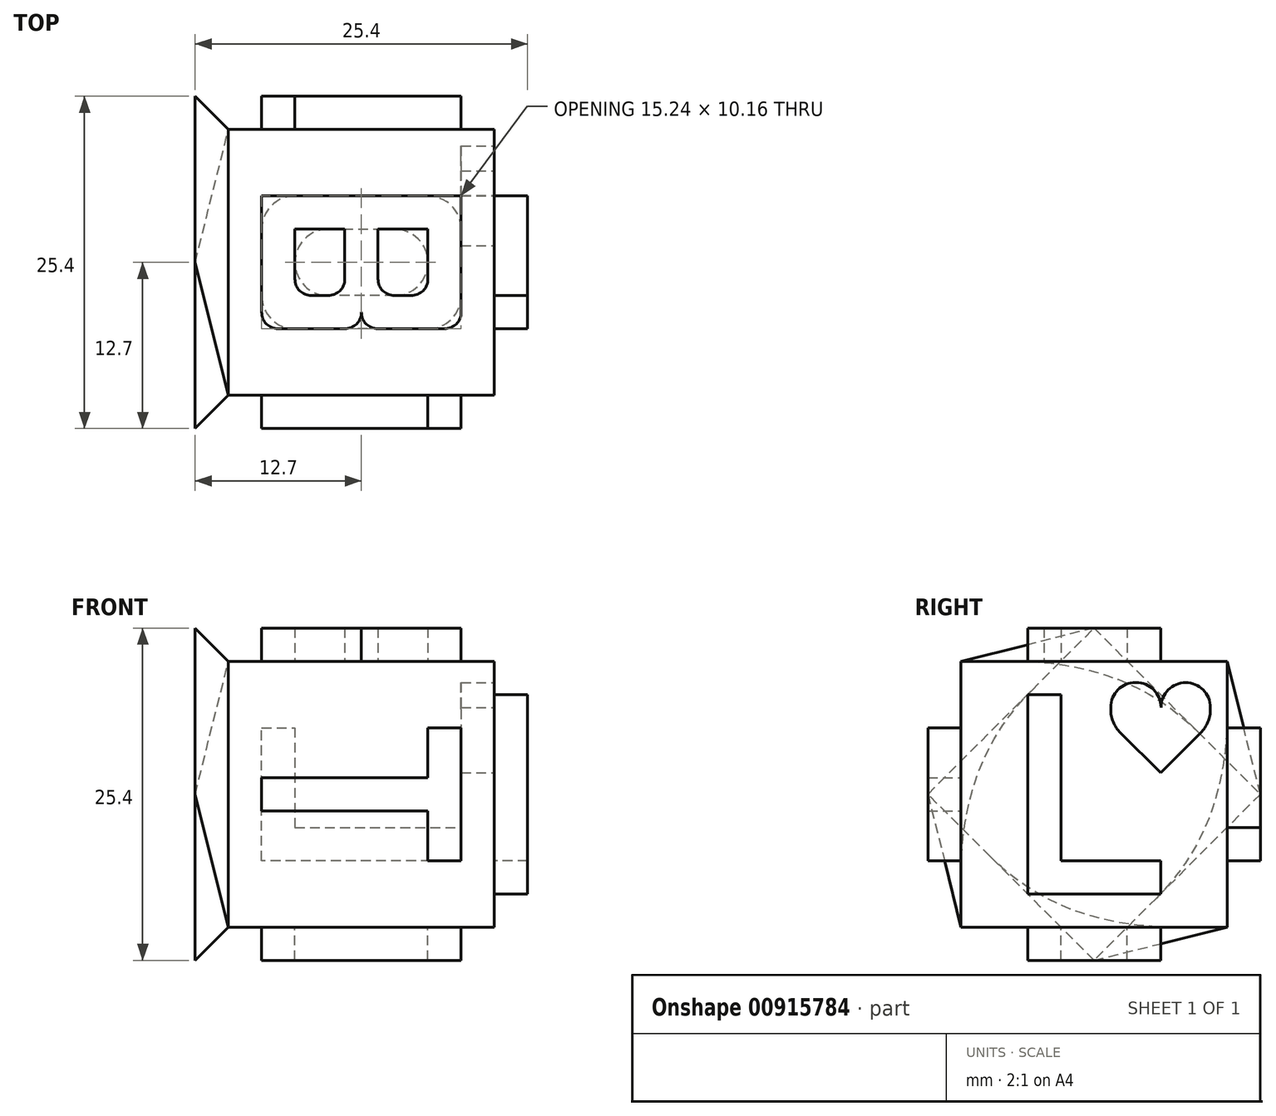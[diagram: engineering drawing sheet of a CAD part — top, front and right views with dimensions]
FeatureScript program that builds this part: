
annotation { "Feature Type Name" : "Feature", "Feature Type Description" : "" }
export const myFeature = defineFeature(function(context is Context, id is Id, definition is map)
    precondition{}
    {
        {
            var Q0;
            Q0=qCreatedBy(makeId("Right.planeOp"),FACE);
            var sketch = newSketch(context, id + "F0", { "sketchPlane" : qUnion([Q0])});
            skLineSegment(sketch, "E0.bottom", {"start": v(10.16, -10.16) * mm, "end": v(-10.16, -10.16) * mm});
            skLineSegment(sketch, "E0.top", {"start": v(10.16, 10.16) * mm, "end": v(-10.16, 10.16) * mm});
            skLineSegment(sketch, "E0.left", {"start": v(10.16, -10.16) * mm, "end": v(10.16, 10.16) * mm});
            skLineSegment(sketch, "E0.right", {"start": v(-10.16, -10.16) * mm, "end": v(-10.16, 10.16) * mm});
            skPoint(sketch, "E0.middle", {"position": v(0, 0) * mm});
            skSolve(sketch);
        }
        {
            var Q0;
            Q0=makeQuery(id+"F0.imprint","IMPRINT",FACE,{"disambiguationData":[TD([[makeQuery(id+"F0.imprint","IMPRINT",EDGE,{"derivedFrom":sQuery(id+"F0.wireOp",EDGE,"E0.bottom")}),-1.0]])]});
            extrude(context, id + "F1", {"entities" : qUnion([Q0]), "depth" : 20.32 * mm, "offsetDistance" : 25.4 * mm});
        }
        {
            var Q0;
            Q0=makeQuery(id+"F1.opExtrude","CAP_FACE",FACE,{"disambiguationData":[OSD([sQuery(id+"F0.wireOp",EDGE,"E0.bottom"),sQuery(id+"F0.wireOp",EDGE,"E0.top"),sQuery(id+"F0.wireOp",EDGE,"E0.left"),sQuery(id+"F0.wireOp",EDGE,"E0.right")])],"isStart":false});
            var sketch = newSketch(context, id + "F2", { "sketchPlane" : qUnion([Q0])});
            skLineSegment(sketch, "E1", {"start": v(-5.08, 7.62) * mm, "end": v(-5.08, -7.62) * mm});
            skLineSegment(sketch, "E2", {"start": v(-5.08, -7.62) * mm, "end": v(5.08, -7.62) * mm});
            skLineSegment(sketch, "E3", {"start": v(5.08, -7.62) * mm, "end": v(5.08, -5.08) * mm});
            skLineSegment(sketch, "E4", {"start": v(5.08, -5.08) * mm, "end": v(-2.54, -5.08) * mm});
            skLineSegment(sketch, "E5", {"start": v(-2.54, -5.08) * mm, "end": v(-2.54, 7.62) * mm});
            skLineSegment(sketch, "E6", {"start": v(-2.54, 7.62) * mm, "end": v(-5.08, 7.62) * mm});
            skSolve(sketch);
        }
        {
            var Q0;
            Q0=makeQuery(id+"F2.imprint","IMPRINT",FACE,{"disambiguationData":[TD([[makeQuery(id+"F2.imprint","IMPRINT",EDGE,{"derivedFrom":sQuery(id+"F2.wireOp",EDGE,"E1")}),1.0]])]});
            extrude(context, id + "F3", {"entities" : qUnion([Q0]), "operationType" : NewBodyOperationType.ADD, "depth" : 2.54 * mm, "offsetDistance" : 25.4 * mm});
        }
        {
            var Q0;
            Q0=makeQuery(id+"F1.opExtrude","SWEPT_FACE",FACE,{"disambiguationData":[OSD([sQuery(id+"F0.wireOp",EDGE,"E0.bottom")])]});
            var sketch = newSketch(context, id + "F4", { "sketchPlane" : qUnion([Q0])});
            skLineSegment(sketch, "E7", {"start": v(15.24, 5.08) * mm, "end": v(5.08, 5.08) * mm});
            skLineSegment(sketch, "E8", {"start": v(2.54, 2.54) * mm, "end": v(2.54, -2.54) * mm});
            skLineSegment(sketch, "E9", {"start": v(5.08, -5.08) * mm, "end": v(15.24, -5.08) * mm});
            skLineSegment(sketch, "E10", {"start": v(17.78, -2.54) * mm, "end": v(17.78, 2.54) * mm});
            skLineSegment(sketch, "E11", {"start": v(12.7, 2.54) * mm, "end": v(7.62, 2.54) * mm});
            skLineSegment(sketch, "E12", {"start": v(5.08, 0) * mm, "end": v(5.08, 0) * mm});
            skLineSegment(sketch, "E13", {"start": v(7.62, -2.54) * mm, "end": v(12.7, -2.54) * mm});
            skLineSegment(sketch, "E14", {"start": v(15.24, 0) * mm, "end": v(15.24, 0) * mm});
            skPoint(sketch, "E15.visualSharp", {"position": v(17.78, 5.08) * mm});
            skArc(sketch, "E15.filletArc", {"start": v(17.78, 2.54) * mm, "mid": v(17.04, 4.34) * mm, "end": v(15.24, 5.08) * mm});
            skPoint(sketch, "E16.visualSharp", {"position": v(17.78, -5.08) * mm});
            skArc(sketch, "E16.filletArc", {"start": v(15.24, -5.08) * mm, "mid": v(17.04, -4.34) * mm, "end": v(17.78, -2.54) * mm});
            skPoint(sketch, "E17.visualSharp", {"position": v(2.54, -5.08) * mm});
            skArc(sketch, "E17.filletArc", {"start": v(2.54, -2.54) * mm, "mid": v(3.28, -4.34) * mm, "end": v(5.08, -5.08) * mm});
            skPoint(sketch, "E18.visualSharp", {"position": v(2.54, 5.08) * mm});
            skArc(sketch, "E18.filletArc", {"start": v(5.08, 5.08) * mm, "mid": v(3.28, 4.34) * mm, "end": v(2.54, 2.54) * mm});
            skArc(sketch, "E19.filletArc", {"start": v(7.62, 2.54) * mm, "mid": v(5.82, 1.8) * mm, "end": v(5.08, 0) * mm});
            skArc(sketch, "E20.filletArc", {"start": v(5.08, 0) * mm, "mid": v(5.82, -1.8) * mm, "end": v(7.62, -2.54) * mm});
            skArc(sketch, "E21.filletArc", {"start": v(12.7, -2.54) * mm, "mid": v(14.5, -1.8) * mm, "end": v(15.24, 0) * mm});
            skArc(sketch, "E22.filletArc", {"start": v(15.24, 0) * mm, "mid": v(14.5, 1.8) * mm, "end": v(12.7, 2.54) * mm});
            skSolve(sketch);
        }
        {
            var Q0;
            Q0=makeQuery(id+"F4.imprint","IMPRINT",FACE,{"disambiguationData":[TD([[makeQuery(id+"F4.imprint","IMPRINT",EDGE,{"derivedFrom":sQuery(id+"F4.wireOp",EDGE,"E7")}),1.0]])]});
            extrude(context, id + "F5", {"entities" : qUnion([Q0]), "operationType" : NewBodyOperationType.ADD, "depth" : 2.54 * mm, "offsetDistance" : 25.4 * mm});
        }
        {
            var Q0;
            Q0=makeQuery(id+"F1.opExtrude","SWEPT_FACE",FACE,{"disambiguationData":[OSD([sQuery(id+"F0.wireOp",EDGE,"E0.right")])]});
            var sketch = newSketch(context, id + "F6", { "sketchPlane" : qUnion([Q0])});
            skLineSegment(sketch, "E23", {"start": v(2.54, 1.27) * mm, "end": v(15.24, 1.27) * mm});
            skLineSegment(sketch, "E24", {"start": v(15.24, 1.27) * mm, "end": v(15.24, 5.08) * mm});
            skLineSegment(sketch, "E25", {"start": v(15.24, 5.08) * mm, "end": v(17.78, 5.08) * mm});
            skLineSegment(sketch, "E26", {"start": v(17.78, 5.08) * mm, "end": v(17.78, -5.08) * mm});
            skLineSegment(sketch, "E27", {"start": v(17.78, -5.08) * mm, "end": v(15.24, -5.08) * mm});
            skLineSegment(sketch, "E28", {"start": v(15.24, -5.08) * mm, "end": v(15.24, -1.27) * mm});
            skLineSegment(sketch, "E29", {"start": v(15.24, -1.27) * mm, "end": v(2.54, -1.27) * mm});
            skLineSegment(sketch, "E30", {"start": v(2.54, -1.27) * mm, "end": v(2.54, 1.27) * mm});
            skSolve(sketch);
        }
        {
            var Q0;
            Q0=makeQuery(id+"F6.imprint","IMPRINT",FACE,{"disambiguationData":[TD([[makeQuery(id+"F6.imprint","IMPRINT",EDGE,{"derivedFrom":sQuery(id+"F6.wireOp",EDGE,"E23")}),-1.0]])]});
            extrude(context, id + "F7", {"entities" : qUnion([Q0]), "operationType" : NewBodyOperationType.ADD, "depth" : 2.54 * mm, "offsetDistance" : 25.4 * mm});
        }
        {
            var Q0;
            Q0=makeQuery(id+"F1.opExtrude","SWEPT_FACE",FACE,{"disambiguationData":[OSD([sQuery(id+"F0.wireOp",EDGE,"E0.top")])]});
            var sketch = newSketch(context, id + "F8", { "sketchPlane" : qUnion([Q0])});
            skLineSegment(sketch, "E31", {"start": v(17.78, 5.08) * mm, "end": v(2.54, 5.08) * mm});
            skLineSegment(sketch, "E32", {"start": v(2.54, 5.08) * mm, "end": v(2.54, -3.81) * mm});
            skLineSegment(sketch, "E33", {"start": v(3.81, -5.08) * mm, "end": v(8.9, -5.08) * mm});
            skLineSegment(sketch, "E34", {"start": v(10.16, -3.81) * mm, "end": v(10.16, 5.08) * mm});
            skLineSegment(sketch, "E35", {"start": v(11.43, -5.08) * mm, "end": v(16.51, -5.08) * mm});
            skLineSegment(sketch, "E36", {"start": v(17.78, -3.81) * mm, "end": v(17.78, 5.08) * mm});
            skLineSegment(sketch, "E37", {"start": v(11.43, 2.54) * mm, "end": v(15.24, 2.54) * mm});
            skLineSegment(sketch, "E38", {"start": v(15.24, 2.54) * mm, "end": v(15.24, -1.27) * mm});
            skLineSegment(sketch, "E39", {"start": v(13.97, -2.54) * mm, "end": v(12.7, -2.54) * mm});
            skLineSegment(sketch, "E40", {"start": v(11.43, -1.27) * mm, "end": v(11.43, 2.54) * mm});
            skLineSegment(sketch, "E41", {"start": v(5.08, 2.54) * mm, "end": v(8.9, 2.54) * mm});
            skLineSegment(sketch, "E42", {"start": v(8.9, 2.54) * mm, "end": v(8.9, -1.27) * mm});
            skLineSegment(sketch, "E43", {"start": v(7.62, -2.54) * mm, "end": v(6.35, -2.54) * mm});
            skLineSegment(sketch, "E44", {"start": v(5.08, -1.27) * mm, "end": v(5.08, 2.54) * mm});
            skPoint(sketch, "E45.visualSharp", {"position": v(10.16, -5.08) * mm});
            skArc(sketch, "E45.filletArc", {"start": v(10.16, -3.8) * mm, "mid": v(10.53, -4.7) * mm, "end": v(11.43, -5.08) * mm});
            skArc(sketch, "E46.filletArc", {"start": v(8.9, -5.08) * mm, "mid": v(9.79, -4.7) * mm, "end": v(10.16, -3.81) * mm});
            skPoint(sketch, "E47.visualSharp", {"position": v(17.78, -5.08) * mm});
            skArc(sketch, "E47.filletArc", {"start": v(16.51, -5.08) * mm, "mid": v(17.4, -4.7) * mm, "end": v(17.78, -3.81) * mm});
            skPoint(sketch, "E48.visualSharp", {"position": v(2.54, -5.08) * mm});
            skArc(sketch, "E48.filletArc", {"start": v(2.54, -3.81) * mm, "mid": v(2.91, -4.7) * mm, "end": v(3.81, -5.08) * mm});
            skPoint(sketch, "E49.visualSharp", {"position": v(11.43, -2.54) * mm});
            skArc(sketch, "E49.filletArc", {"start": v(11.43, -1.27) * mm, "mid": v(11.8, -2.17) * mm, "end": v(12.7, -2.54) * mm});
            skPoint(sketch, "E50.visualSharp", {"position": v(15.24, -2.54) * mm});
            skArc(sketch, "E50.filletArc", {"start": v(13.97, -2.54) * mm, "mid": v(14.87, -2.17) * mm, "end": v(15.24, -1.27) * mm});
            skPoint(sketch, "E51.visualSharp", {"position": v(8.9, -2.54) * mm});
            skArc(sketch, "E51.filletArc", {"start": v(7.62, -2.54) * mm, "mid": v(8.52, -2.17) * mm, "end": v(8.9, -1.27) * mm});
            skPoint(sketch, "E52.visualSharp", {"position": v(5.08, -2.54) * mm});
            skArc(sketch, "E52.filletArc", {"start": v(5.08, -1.27) * mm, "mid": v(5.45, -2.17) * mm, "end": v(6.35, -2.54) * mm});
            skSolve(sketch);
        }
        {
            var Q0;
            {var subQ2=sQuery(id+"F8.wireOp",EDGE,"E34");Q0=makeQuery(id+"F8.imprint","IMPRINT",FACE,{"disambiguationData":[TD([[makeQuery(id+"F8.imprint","IMPRINT",EDGE,{"derivedFrom":subQ2}),-1.0]])]});}
            var Q1;
            {var subQ0=sQuery(id+"F8.wireOp",EDGE,"E32");Q1=makeQuery(id+"F8.imprint","IMPRINT",FACE,{"disambiguationData":[TD([[makeQuery(id+"F8.imprint","IMPRINT",EDGE,{"derivedFrom":subQ0}),1.0]])]});}
            extrude(context, id + "F9", {"entities" : qUnion([Q0, Q1]), "operationType" : NewBodyOperationType.ADD, "depth" : 2.54 * mm, "offsetDistance" : 25.4 * mm});
        }
        {
            var Q0;
            Q0=makeQuery(id+"F1.opExtrude","SWEPT_FACE",FACE,{"disambiguationData":[OSD([sQuery(id+"F0.wireOp",EDGE,"E0.left")])]});
            var sketch = newSketch(context, id + "F10", { "sketchPlane" : qUnion([Q0])});
            skLineSegment(sketch, "E53", {"start": v(-17.78, -5.08) * mm, "end": v(-2.54, -5.08) * mm});
            skLineSegment(sketch, "E54", {"start": v(-2.54, -5.08) * mm, "end": v(-2.54, 5.08) * mm});
            skLineSegment(sketch, "E55", {"start": v(-2.54, 5.08) * mm, "end": v(-5.08, 5.08) * mm});
            skLineSegment(sketch, "E56", {"start": v(-5.08, 5.08) * mm, "end": v(-5.08, -2.54) * mm});
            skLineSegment(sketch, "E57", {"start": v(-5.08, -2.54) * mm, "end": v(-17.78, -2.54) * mm});
            skLineSegment(sketch, "E58", {"start": v(-17.78, -2.54) * mm, "end": v(-17.78, -5.08) * mm});
            skSolve(sketch);
        }
        {
            var Q0;
            Q0=makeQuery(id+"F10.imprint","IMPRINT",FACE,{"disambiguationData":[TD([[makeQuery(id+"F10.imprint","IMPRINT",EDGE,{"derivedFrom":sQuery(id+"F10.wireOp",EDGE,"E53")}),1.0]])]});
            extrude(context, id + "F11", {"entities" : qUnion([Q0]), "operationType" : NewBodyOperationType.ADD, "depth" : 2.54 * mm, "offsetDistance" : 25.4 * mm});
        }
        {
            var Q0;
            Q0=makeQuery(id+"F1.opExtrude","CAP_FACE",FACE,{"disambiguationData":[OSD([sQuery(id+"F0.wireOp",EDGE,"E0.bottom"),sQuery(id+"F0.wireOp",EDGE,"E0.top"),sQuery(id+"F0.wireOp",EDGE,"E0.left"),sQuery(id+"F0.wireOp",EDGE,"E0.right")])],"isStart":true});
            cPlane(context, id + "F12", {"entities" : qUnion([Q0]), "cplaneType" : CPlaneType.OFFSET, "offset" : 2.54 * mm, "width" : 152.4 * mm, "height" : 152.4 * mm});
        }
        {
            var Q0;
            Q0=qCreatedBy(id+"F12.planeOp",FACE);
            var sketch = newSketch(context, id + "F13", { "sketchPlane" : qUnion([Q0])});
            skLineSegment(sketch, "E59", {"start": v(0, 12.7) * mm, "end": v(-12.7, 0) * mm});
            skLineSegment(sketch, "E60", {"start": v(-12.7, 0) * mm, "end": v(0, -12.7) * mm});
            skLineSegment(sketch, "E61", {"start": v(0, -12.7) * mm, "end": v(12.7, 0) * mm});
            skLineSegment(sketch, "E62", {"start": v(12.7, 0) * mm, "end": v(0, 12.7) * mm});
            skSolve(sketch);
        }
        {
            var Q1;
            Q1=makeQuery(id+"F13.imprint","IMPRINT",FACE,{"disambiguationData":[TD([[makeQuery(id+"F13.imprint","IMPRINT",EDGE,{"derivedFrom":sQuery(id+"F13.wireOp",EDGE,"E59")}),1.0]])]});
            var Q2;
            Q2=makeQuery(id+"F1.opExtrude","CAP_FACE",FACE,{"disambiguationData":[OSD([sQuery(id+"F0.wireOp",EDGE,"E0.bottom"),sQuery(id+"F0.wireOp",EDGE,"E0.top"),sQuery(id+"F0.wireOp",EDGE,"E0.left"),sQuery(id+"F0.wireOp",EDGE,"E0.right")])],"isStart":true});
            loft(context, id + "F14", {"operationType" : NewBodyOperationType.ADD, "sheetProfilesArray" : [{ "sheetProfileEntities" : qUnion([Q1]) }, { "sheetProfileEntities" : qUnion([Q2]) }]});
        }
        {
            var Q0;
            Q0=makeQuery(id+"F1.opExtrude","CAP_FACE",FACE,{"disambiguationData":[OSD([sQuery(id+"F0.wireOp",EDGE,"E0.bottom"),sQuery(id+"F0.wireOp",EDGE,"E0.top"),sQuery(id+"F0.wireOp",EDGE,"E0.left"),sQuery(id+"F0.wireOp",EDGE,"E0.right")])],"isStart":false});
            var sketch = newSketch(context, id + "F15", { "sketchPlane" : qUnion([Q0])});
            skLineSegment(sketch, "E63.bottom", {"start": v(10.16, 10.16) * mm, "end": v(0, 10.16) * mm});
            skLineSegment(sketch, "E63.top", {"start": v(10.16, 0) * mm, "end": v(0, 0) * mm});
            skLineSegment(sketch, "E63.left", {"start": v(10.16, 10.16) * mm, "end": v(10.16, 0) * mm});
            skLineSegment(sketch, "E63.right", {"start": v(0, 10.16) * mm, "end": v(0, 0) * mm});
            skSolve(sketch);
        }
        {
            var Q0;
            Q0=makeQuery(id+"F15.imprint","IMPRINT",FACE,{"disambiguationData":[TD([[makeQuery(id+"F15.imprint","IMPRINT",EDGE,{"derivedFrom":sQuery(id+"F15.wireOp",EDGE,"E63.bottom")}),1.0]])]});
            cPlane(context, id + "F16", {"entities" : qUnion([Q0]), "cplaneType" : CPlaneType.OFFSET, "offset" : 1.27 * mm, "width" : 152.4 * mm, "height" : 152.4 * mm});
        }
        {
            var Q0;
            Q0=qCreatedBy(id+"F16.planeOp",FACE);
            var sketch = newSketch(context, id + "F17", { "sketchPlane" : qUnion([Q0])});
            skLineSegment(sketch, "E64", {"start": v(5.08, 1.62) * mm, "end": v(8.15, 4.7) * mm});
            skLineSegment(sketch, "E65", {"start": v(5.08, 1.62) * mm, "end": v(2.01, 4.7) * mm});
            skLineSegment(sketch, "E66", {"start": v(1.27, 6.49) * mm, "end": v(1.27, 6.63) * mm});
            skLineSegment(sketch, "E67", {"start": v(3.18, 8.54) * mm, "end": v(3.2, 8.54) * mm});
            skPoint(sketch, "E68.visualSharp", {"position": v(1.27, 8.54) * mm});
            skArc(sketch, "E68.filletArc", {"start": v(3.18, 8.54) * mm, "mid": v(1.83, 7.98) * mm, "end": v(1.27, 6.63) * mm});
            skPoint(sketch, "E69.visualSharp", {"position": v(5.11, 8.54) * mm});
            skArc(sketch, "E69.filletArc", {"start": v(5.11, 6.63) * mm, "mid": v(4.55, 7.98) * mm, "end": v(3.2, 8.54) * mm});
            skPoint(sketch, "E70.visualSharp", {"position": v(1.27, 5.43) * mm});
            skArc(sketch, "E70.filletArc", {"start": v(1.27, 6.49) * mm, "mid": v(1.46, 5.51) * mm, "end": v(2.01, 4.7) * mm});
            skLineSegment(sketch, "E71", {"start": v(5.11, 6.63) * mm, "end": v(5.11, 6.63) * mm});
            skLineSegment(sketch, "E72", {"start": v(8.9, 6.63) * mm, "end": v(8.9, 6.49) * mm});
            skLineSegment(sketch, "E73", {"start": v(7.02, 8.54) * mm, "end": v(6.99, 8.54) * mm});
            skArc(sketch, "E74.filletArc", {"start": v(7.02, 8.54) * mm, "mid": v(5.67, 7.98) * mm, "end": v(5.11, 6.63) * mm});
            skPoint(sketch, "E75.visualSharp", {"position": v(8.9, 8.54) * mm});
            skArc(sketch, "E75.filletArc", {"start": v(8.9, 6.63) * mm, "mid": v(8.33, 7.98) * mm, "end": v(6.99, 8.54) * mm});
            skPoint(sketch, "E76.visualSharp", {"position": v(8.9, 5.43) * mm});
            skArc(sketch, "E76.filletArc", {"start": v(8.15, 4.7) * mm, "mid": v(8.7, 5.51) * mm, "end": v(8.9, 6.49) * mm});
            skPoint(sketch, "E77.end.orphan", {"position": v(5.08, 5.43) * mm});
            skSolve(sketch);
        }
        {
            var Q0;
            Q0=makeQuery(id+"F17.imprint","IMPRINT",FACE,{"disambiguationData":[TD([[makeQuery(id+"F17.imprint","IMPRINT",EDGE,{"derivedFrom":sQuery(id+"F17.wireOp",EDGE,"E64")}),1.0]])]});
            extrude(context, id + "F18", {"entities" : qUnion([Q0]), "operationType" : NewBodyOperationType.ADD, "oppositeDirection" : true, "depth" : 1.27 * mm, "offsetDistance" : 25.4 * mm, "hasSecondDirection" : true, "secondDirectionOppositeDirection" : false, "secondDirectionDepth" : 1.27 * mm});
        }
        {
            var Q0;
            Q0=makeQuery(id+"F18.opExtrude","CAP_FACE",FACE,{"disambiguationData":[OSD([sQuery(id+"F17.wireOp",EDGE,"E64"),sQuery(id+"F17.wireOp",EDGE,"E65"),sQuery(id+"F17.wireOp",EDGE,"E66"),sQuery(id+"F17.wireOp",EDGE,"E67"),sQuery(id+"F17.wireOp",EDGE,"E68.filletArc"),sQuery(id+"F17.wireOp",EDGE,"E69.filletArc"),sQuery(id+"F17.wireOp",EDGE,"E70.filletArc"),sQuery(id+"F17.wireOp",EDGE,"E72"),sQuery(id+"F17.wireOp",EDGE,"E74.filletArc"),sQuery(id+"F17.wireOp",EDGE,"E75.filletArc"),sQuery(id+"F17.wireOp",EDGE,"E76.filletArc")])],"isStart":true});
            extrude(context, id + "F19", {"entities" : qUnion([Q0]), "operationType" : NewBodyOperationType.REMOVE, "oppositeDirection" : true, "depth" : 5.08 * mm, "offsetDistance" : 25.4 * mm});
        }
    });
